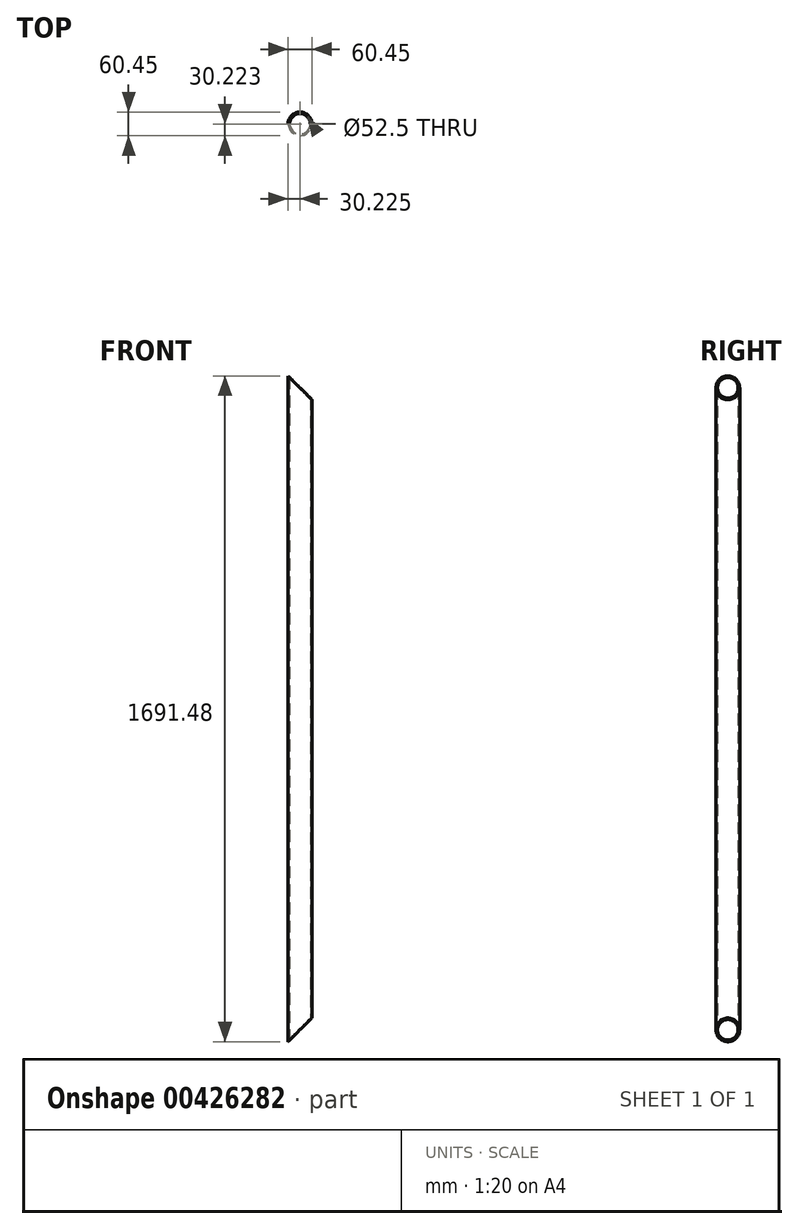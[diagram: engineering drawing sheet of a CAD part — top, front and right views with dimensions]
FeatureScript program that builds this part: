
annotation { "Feature Type Name" : "Feature", "Feature Type Description" : "" }
export const myFeature = defineFeature(function(context is Context, id is Id, definition is map)
    precondition{}
    {
        {
            var Q0;
            Q0=qCreatedBy(makeId("Top.planeOp"),FACE);
            var sketch = newSketch(context, id + "F0", { "sketchPlane" : qUnion([Q0])});
            skCircle(sketch, "E0", {"center": v(-125.82, -56.06) * mm, "radius": 30.23 * mm});
            skCircle(sketch, "E1", {"center": v(-125.82, -56.06) * mm, "radius": 26.25 * mm});
            skSolve(sketch);
        }
        {
            var Q0;
            Q0=makeQuery(id+"F0.imprint","IMPRINT",FACE,{"disambiguationData":[TD([[makeQuery(id+"F0.imprint","IMPRINT",EDGE,{"derivedFrom":sQuery(id+"F0.wireOp",EDGE,"E0")}),1.0]])]});
            extrude(context, id + "F1", {"entities" : qUnion([Q0]), "depth" : 1695.45 * mm});
        }
        {
            var Q0;
            Q0=qCreatedBy(makeId("Front.planeOp"),FACE);
            var sketch = newSketch(context, id + "F2", { "sketchPlane" : qUnion([Q0])});
            skLineSegment(sketch, "E2", {"start": v(-159.12, 0) * mm, "end": v(-89.99, 69.13) * mm});
            skLineSegment(sketch, "E3", {"start": v(-88.82, 0) * mm, "end": v(-159.12, 0) * mm});
            skLineSegment(sketch, "E4", {"start": v(-89.99, 69.13) * mm, "end": v(-88.82, 0) * mm});
            skSolve(sketch);
        }
        {
            var Q0;
            Q0=makeQuery(id+"F2.imprint","IMPRINT",FACE,{"disambiguationData":[TD([[makeQuery(id+"F2.imprint","IMPRINT",EDGE,{"derivedFrom":sQuery(id+"F2.wireOp",EDGE,"E2")}),-1.0]])]});
            extrude(context, id + "F3", {"entities" : qUnion([Q0]), "operationType" : NewBodyOperationType.REMOVE, "depth" : 103.12 * mm});
        }
        {
            var Q0;
            Q0=qCreatedBy(makeId("Front.planeOp"),FACE);
            var sketch = newSketch(context, id + "F4", { "sketchPlane" : qUnion([Q0])});
            skLineSegment(sketch, "E5", {"start": v(-163.89, 1702.4) * mm, "end": v(-93.4, 1631.93) * mm});
            skLineSegment(sketch, "E6", {"start": v(-93.4, 1631.93) * mm, "end": v(-93.4, 1702.4) * mm});
            skLineSegment(sketch, "E7", {"start": v(-163.89, 1702.4) * mm, "end": v(-93.4, 1702.4) * mm});
            skSolve(sketch);
        }
        {
            var Q0;
            Q0=makeQuery(id+"F4.imprint","IMPRINT",FACE,{"disambiguationData":[TD([[makeQuery(id+"F4.imprint","IMPRINT",EDGE,{"derivedFrom":sQuery(id+"F4.wireOp",EDGE,"E5")}),1.0]])]});
            extrude(context, id + "F5", {"entities" : qUnion([Q0]), "operationType" : NewBodyOperationType.REMOVE, "depth" : 124.97 * mm});
        }
    });
